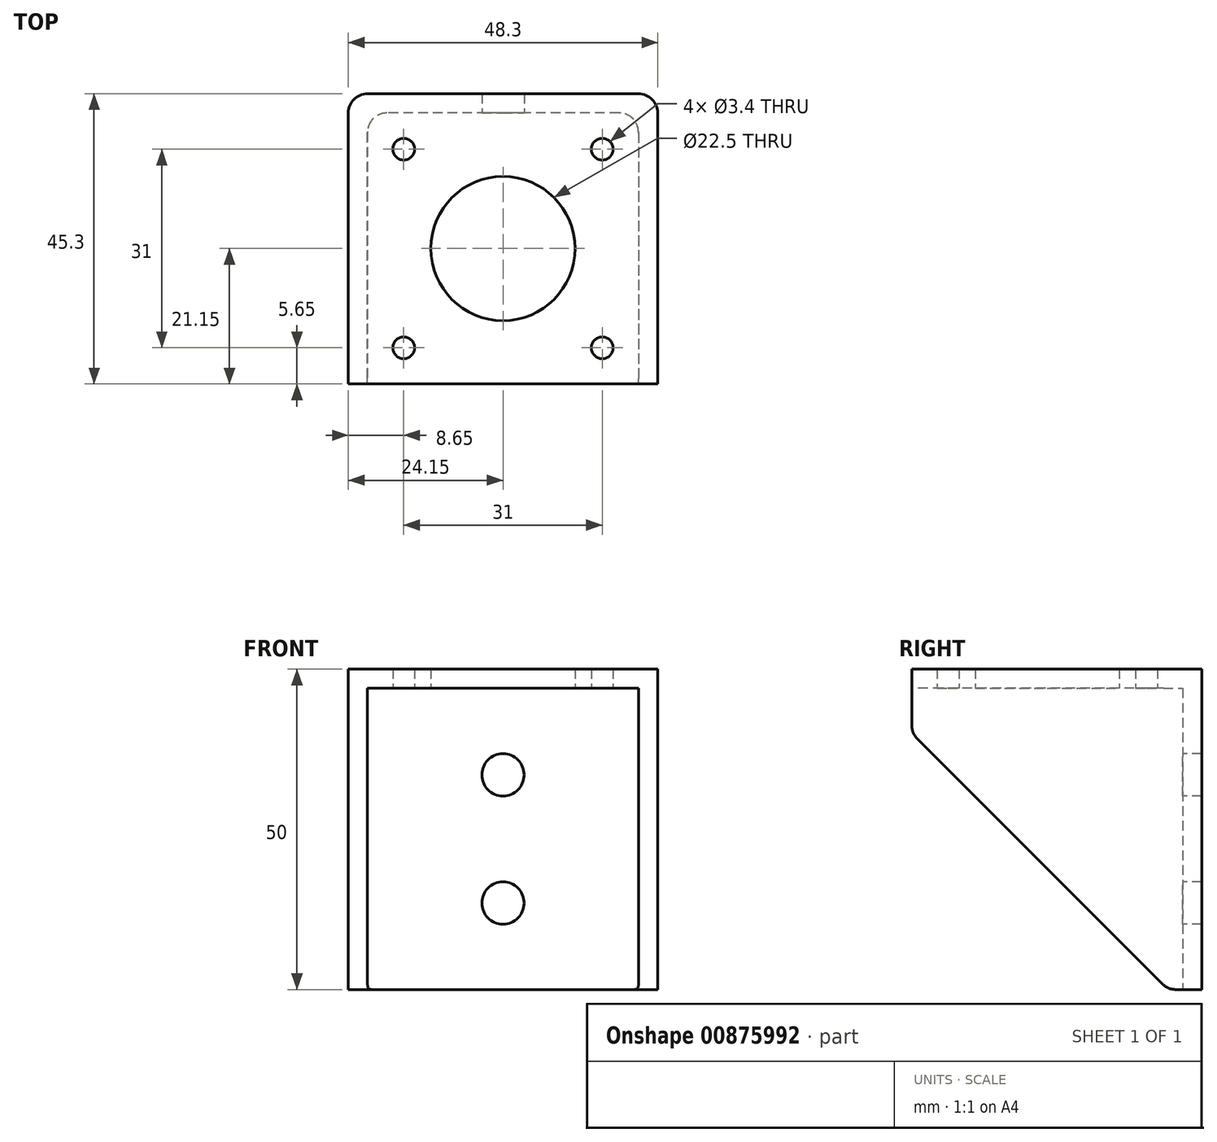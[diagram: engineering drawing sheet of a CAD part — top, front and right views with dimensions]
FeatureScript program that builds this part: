
annotation { "Feature Type Name" : "Feature", "Feature Type Description" : "" }
export const myFeature = defineFeature(function(context is Context, id is Id, definition is map)
    precondition{}
    {
        {
            assignVariable(context, id + "F0", {"name" : "wallThickness", "anyValue" : 3});
        }
        {
            var Q0;
            Q0=qCreatedBy(makeId("Top.planeOp"),FACE);
            var sketch = newSketch(context, id + "F1", { "sketchPlane" : qUnion([Q0])});
            skLineSegment(sketch, "E0.bottom", {"start": v(21.15, 21.15) * mm, "end": v(-21.15, 21.15) * mm});
            skLineSegment(sketch, "E0.top", {"start": v(21.15, -21.15) * mm, "end": v(-21.15, -21.15) * mm});
            skLineSegment(sketch, "E0.left", {"start": v(21.15, 21.15) * mm, "end": v(21.15, -21.15) * mm});
            skLineSegment(sketch, "E0.right", {"start": v(-21.15, 21.15) * mm, "end": v(-21.15, -21.15) * mm});
            skPoint(sketch, "E0.middle", {"position": v(0, 0) * mm});
            skLineSegment(sketch, "E1.bottom", {"start": v(15.5, 15.5) * mm, "end": v(-15.5, 15.5) * mm, "construction": true});
            skLineSegment(sketch, "E1.top", {"start": v(15.5, -15.5) * mm, "end": v(-15.5, -15.5) * mm, "construction": true});
            skLineSegment(sketch, "E1.left", {"start": v(15.5, 15.5) * mm, "end": v(15.5, -15.5) * mm, "construction": true});
            skLineSegment(sketch, "E1.right", {"start": v(-15.5, 15.5) * mm, "end": v(-15.5, -15.5) * mm, "construction": true});
            skCircle(sketch, "E2", {"center": v(-15.5, 15.5) * mm, "radius": 1.63 * mm});
            skCircle(sketch, "E3", {"center": v(15.5, 15.5) * mm, "radius": 1.63 * mm});
            skCircle(sketch, "E4", {"center": v(15.5, -15.5) * mm, "radius": 1.63 * mm});
            skCircle(sketch, "E5", {"center": v(-15.5, -15.5) * mm, "radius": 1.63 * mm});
            skLineSegment(sketch, "E6.bottom", {"start": v(24.15, 24.15) * mm, "end": v(-24.15, 24.15) * mm});
            skLineSegment(sketch, "E6.top", {"start": v(24.15, -21.15) * mm, "end": v(-24.15, -21.15) * mm});
            skLineSegment(sketch, "E6.left", {"start": v(24.15, 24.15) * mm, "end": v(24.15, -21.15) * mm});
            skLineSegment(sketch, "E6.right", {"start": v(-24.15, 24.15) * mm, "end": v(-24.15, -21.15) * mm});
            skSolve(sketch);
        }
        {
            var Q0;
            Q0=makeQuery(id+"F1.imprint","IMPRINT",FACE,{"disambiguationData":[TD([[makeQuery(id+"F1.imprint","IMPRINT",EDGE,{"derivedFrom":sQuery(id+"F1.wireOp",EDGE,"E0.bottom")}),1.0]])]});
            var Q1;
            Q1=makeQuery(id+"F1.imprint","IMPRINT",FACE,{"disambiguationData":[TD([[makeQuery(id+"F1.imprint","IMPRINT",EDGE,{"derivedFrom":sQuery(id+"F1.wireOp",EDGE,"E2")}),1.0]])]});
            var Q2;
            Q2=makeQuery(id+"F1.imprint","IMPRINT",FACE,{"disambiguationData":[TD([[makeQuery(id+"F1.imprint","IMPRINT",EDGE,{"derivedFrom":sQuery(id+"F1.wireOp",EDGE,"E3")}),1.0]])]});
            var Q3;
            Q3=makeQuery(id+"F1.imprint","IMPRINT",FACE,{"disambiguationData":[TD([[makeQuery(id+"F1.imprint","IMPRINT",EDGE,{"derivedFrom":sQuery(id+"F1.wireOp",EDGE,"E5")}),1.0]])]});
            var Q4;
            Q4=makeQuery(id+"F1.imprint","IMPRINT",FACE,{"disambiguationData":[TD([[makeQuery(id+"F1.imprint","IMPRINT",EDGE,{"derivedFrom":sQuery(id+"F1.wireOp",EDGE,"E4")}),1.0]])]});
            var Q5;
            Q5=makeQuery(id+"F1.imprint","IMPRINT",FACE,{"disambiguationData":[TD([[makeQuery(id+"F1.imprint","IMPRINT",EDGE,{"derivedFrom":sQuery(id+"F1.wireOp",EDGE,"E0.bottom")}),-1.0]])]});
            extrude(context, id + "F2", {"entities" : qUnion([Q0, Q1, Q2, Q3, Q4, Q5]), "depth" : 50 * mm, "offsetDistance" : 25 * mm});
        }
        {
            var Q0;
            Q0=makeQuery(id+"F2.opExtrude","SWEPT_FACE",FACE,{"disambiguationData":[OSD([sQuery(id+"F1.wireOp",EDGE,"E6.top")])]});
            var sketch = newSketch(context, id + "F3", { "sketchPlane" : qUnion([Q0])});
            skLineSegment(sketch, "E7", {"start": v(0, 50) * mm, "end": v(0, 47) * mm, "construction": true});
            skLineSegment(sketch, "E8", {"start": v(0, 47) * mm, "end": v(0, 33.5) * mm, "construction": true});
            skLineSegment(sketch, "E9", {"start": v(0, 33.5) * mm, "end": v(0, 13.5) * mm, "construction": true});
            skLineSegment(sketch, "E10", {"start": v(0, 13.5) * mm, "end": v(0, 0) * mm, "construction": true});
            skSolve(sketch);
        }
        {
            var Q0;
            Q0=makeQuery(id+"F2.opExtrude","SWEPT_FACE",FACE,{"disambiguationData":[OSD([sQuery(id+"F1.wireOp",EDGE,"E6.top")])]});
            var Q1;
            Q1=makeQuery(id+"F2.opExtrude","CAP_FACE",FACE,{"disambiguationData":[OSD([sQuery(id+"F1.wireOp",EDGE,"E6.bottom"),sQuery(id+"F1.wireOp",EDGE,"E6.top"),sQuery(id+"F1.wireOp",EDGE,"E6.left"),sQuery(id+"F1.wireOp",EDGE,"E6.right")])],"isStart":true});
            shell(context, id + "F4", {"entities" : qUnion([Q0, Q1]), "thickness" : (getVariable(context, 'wallThickness')) * mm});
        }
        {
            var Q0;
            Q0=sQuery(id+"F1.wireOp",VERTEX,"E1.top.end");
            var Q1;
            Q1=sQuery(id+"F1.wireOp",VERTEX,"E1.top.start");
            var Q2;
            Q2=sQuery(id+"F1.wireOp",VERTEX,"E1.bottom.start");
            var Q3;
            Q3=sQuery(id+"F1.wireOp",VERTEX,"E1.bottom.end");
            var Q4;
            Q4=makeQuery(id+"F2.opExtrude","SWEPT_BODY",BODY,{"disambiguationData":[OSD([sQuery(id+"F1.wireOp",EDGE,"E6.bottom"),sQuery(id+"F1.wireOp",EDGE,"E6.top"),sQuery(id+"F1.wireOp",EDGE,"E6.left"),sQuery(id+"F1.wireOp",EDGE,"E6.right")])]});
            hole(context, id + "F5", {"style" : HoleStyle.SIMPLE, "endStyle" : HoleEndStyle.THROUGH, "oppositeDirection" : true, "standardTappedOrClearance" : lookupTablePath({ "fit" : "Normal", "standard" : "ISO", "size" : "M3", "type" : "Clearance" }), "standardBlindInLast" : lookupTablePath({ "fit" : "Normal", "standard" : "ISO", "size" : "M3", "type" : "Clearance" }), "holeDiameter" : 3.4 * mm, "majorDiameter" : 5 * mm, "isTappedThrough" : true, "tappedDepth" : 18.5 * mm, "tapClearance" : 3, "locations" : qUnion([Q0, Q1, Q2, Q3]), "scope" : qUnion([Q4])});
        }
        {
            var Q0;
            Q0=sQuery(id+"F3.wireOp",VERTEX,"E8.end");
            var Q1;
            Q1=sQuery(id+"F3.wireOp",VERTEX,"E9.end");
            var Q2;
            Q2=makeQuery(id+"F2.opExtrude","SWEPT_BODY",BODY,{"disambiguationData":[OSD([sQuery(id+"F1.wireOp",EDGE,"E6.bottom"),sQuery(id+"F1.wireOp",EDGE,"E6.top"),sQuery(id+"F1.wireOp",EDGE,"E6.left"),sQuery(id+"F1.wireOp",EDGE,"E6.right")])]});
            hole(context, id + "F6", {"style" : HoleStyle.SIMPLE, "endStyle" : HoleEndStyle.THROUGH, "standardTappedOrClearance" : lookupTablePath({ "fit" : "Normal", "standard" : "ISO", "size" : "M6", "type" : "Clearance" }), "standardBlindInLast" : lookupTablePath({ "fit" : "Normal", "standard" : "ISO", "size" : "M6", "type" : "Clearance" }), "holeDiameter" : 6.6 * mm, "majorDiameter" : 5 * mm, "isTappedThrough" : true, "tappedDepth" : 18.5 * mm, "tapClearance" : 3, "locations" : qUnion([Q0, Q1]), "scope" : qUnion([Q2])});
        }
        {
            var Q0;
            Q0=sQuery(id+"F1.wireOp",VERTEX,"E0.middle");
            var Q1;
            Q1=makeQuery(id+"F2.opExtrude","SWEPT_BODY",BODY,{"disambiguationData":[OSD([sQuery(id+"F1.wireOp",EDGE,"E6.bottom"),sQuery(id+"F1.wireOp",EDGE,"E6.top"),sQuery(id+"F1.wireOp",EDGE,"E6.left"),sQuery(id+"F1.wireOp",EDGE,"E6.right")])]});
            hole(context, id + "F7", {"style" : HoleStyle.SIMPLE, "endStyle" : HoleEndStyle.THROUGH, "oppositeDirection" : true, "holeDiameter" : 22.5 * mm, "majorDiameter" : 5 * mm, "isTappedThrough" : true, "tappedDepth" : 18.5 * mm, "tapClearance" : 3, "locations" : qUnion([Q0]), "scope" : qUnion([Q1])});
        }
        {
            var Q0;
            {var subQ0=sQuery(id+"F1.wireOp",EDGE,"E6.top");Q0=makeQuery(id+"F4.opShell","OFFSET_EDGE",EDGE,{"disambiguationData":[OSD([subQ0]),TDD([makeQuery(id+"F2.opExtrude","CAP_EDGE",EDGE,{"disambiguationData":[OSD([subQ0])],"isStart":true})])]});}
            var Q1;
            Q1=makeQuery(id+"F2.opExtrude","CAP_EDGE",EDGE,{"disambiguationData":[OSD([sQuery(id+"F1.wireOp",EDGE,"E6.top")])],"isStart":true});
            chamfer(context, id + "F8", {"entities" : qUnion([Q0, Q1]), "width" : 40 * mm, "tangentPropagation" : true});
        }
        {
            var Q0;
            {var subQ0=sQuery(id+"F1.wireOp",EDGE,"E6.top");Q0=makeQuery(id+"F8.opChamfer","BLEND_EDGE",EDGE,{"blendedFrom":[makeQuery(id+"F4.opShell","OFFSET_EDGE",EDGE,{"disambiguationData":[OSD([subQ0]),TDD([makeQuery(id+"F2.opExtrude","CAP_EDGE",EDGE,{"disambiguationData":[OSD([subQ0])],"isStart":true})])]}),makeQuery(id+"F2.opExtrude","SWEPT_FACE",FACE,{"disambiguationData":[OSD([subQ0])]})],"blendedInto":[makeQuery(id+"F2.opExtrude","SWEPT_FACE",FACE,{"disambiguationData":[OSD([subQ0])]})]});}
            var Q1;
            {var subQ0=sQuery(id+"F1.wireOp",EDGE,"E6.top");Q1=makeQuery(id+"F8.opChamfer","BLEND_EDGE",EDGE,{"blendedFrom":[makeQuery(id+"F2.opExtrude","CAP_EDGE",EDGE,{"disambiguationData":[OSD([subQ0])],"isStart":true}),makeQuery(id+"F2.opExtrude","SWEPT_FACE",FACE,{"disambiguationData":[OSD([subQ0])]})],"blendedInto":[makeQuery(id+"F2.opExtrude","SWEPT_FACE",FACE,{"disambiguationData":[OSD([subQ0])]})]});}
            var Q2;
            {var subQ0=sQuery(id+"F1.wireOp",EDGE,"E6.top");Q2=makeQuery(id+"F8.opChamfer","BLEND_EDGE",EDGE,{"blendedFrom":[makeQuery(id+"F4.opShell","OFFSET_EDGE",EDGE,{"disambiguationData":[OSD([subQ0]),TDD([makeQuery(id+"F2.opExtrude","CAP_EDGE",EDGE,{"disambiguationData":[OSD([subQ0])],"isStart":true})])]}),makeQuery(id+"F2.opExtrude","CAP_FACE",FACE,{"disambiguationData":[OSD([sQuery(id+"F1.wireOp",EDGE,"E6.bottom"),subQ0,sQuery(id+"F1.wireOp",EDGE,"E6.left"),sQuery(id+"F1.wireOp",EDGE,"E6.right")])],"isStart":true})],"blendedInto":[makeQuery(id+"F2.opExtrude","CAP_FACE",FACE,{"disambiguationData":[OSD([sQuery(id+"F1.wireOp",EDGE,"E6.bottom"),subQ0,sQuery(id+"F1.wireOp",EDGE,"E6.left"),sQuery(id+"F1.wireOp",EDGE,"E6.right")])],"isStart":true})]});}
            var Q3;
            {var subQ0=sQuery(id+"F1.wireOp",EDGE,"E6.top");Q3=makeQuery(id+"F8.opChamfer","BLEND_EDGE",EDGE,{"blendedFrom":[makeQuery(id+"F2.opExtrude","CAP_EDGE",EDGE,{"disambiguationData":[OSD([subQ0])],"isStart":true}),makeQuery(id+"F2.opExtrude","CAP_FACE",FACE,{"disambiguationData":[OSD([sQuery(id+"F1.wireOp",EDGE,"E6.bottom"),subQ0,sQuery(id+"F1.wireOp",EDGE,"E6.left"),sQuery(id+"F1.wireOp",EDGE,"E6.right")])],"isStart":true})],"blendedInto":[makeQuery(id+"F2.opExtrude","CAP_FACE",FACE,{"disambiguationData":[OSD([sQuery(id+"F1.wireOp",EDGE,"E6.bottom"),subQ0,sQuery(id+"F1.wireOp",EDGE,"E6.left"),sQuery(id+"F1.wireOp",EDGE,"E6.right")])],"isStart":true})]});}
            var Q4;
            Q4=makeQuery(id+"F4.opShell","OFFSET_EDGE",EDGE,{"disambiguationData":[OSD([sQuery(id+"F1.wireOp",EDGE,"E6.bottom"),sQuery(id+"F1.wireOp",EDGE,"E6.right")])]});
            var Q5;
            Q5=makeQuery(id+"F4.opShell","OFFSET_EDGE",EDGE,{"disambiguationData":[OSD([sQuery(id+"F1.wireOp",EDGE,"E6.bottom"),sQuery(id+"F1.wireOp",EDGE,"E6.left")])]});
            var Q6;
            Q6=makeQuery(id+"F2.opExtrude","SWEPT_EDGE",EDGE,{"disambiguationData":[OSD([sQuery(id+"F1.wireOp",EDGE,"E6.bottom"),sQuery(id+"F1.wireOp",EDGE,"E6.right")])]});
            var Q7;
            Q7=makeQuery(id+"F2.opExtrude","SWEPT_EDGE",EDGE,{"disambiguationData":[OSD([sQuery(id+"F1.wireOp",EDGE,"E6.bottom"),sQuery(id+"F1.wireOp",EDGE,"E6.left")])]});
            fillet(context, id + "F9", {"entities" : qUnion([Q0, Q1, Q2, Q3, Q4, Q5, Q6, Q7]), "radius" : 3 * mm, "tangentPropagation" : true, "allowEdgeOverflow" : false});
        }
    });
